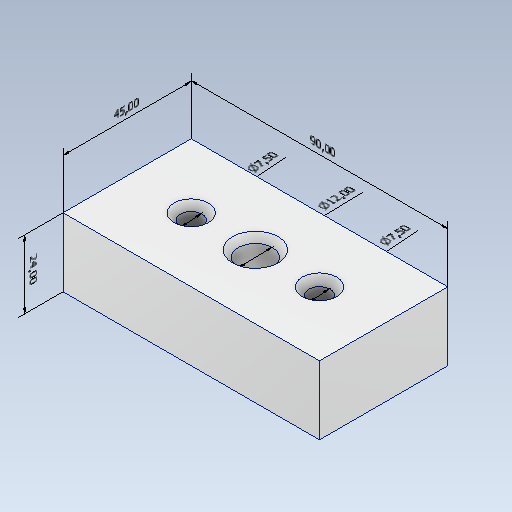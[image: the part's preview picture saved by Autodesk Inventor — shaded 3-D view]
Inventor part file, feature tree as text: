
AUTODESK INVENTOR PART (.ipt)
format: ipt  version: 2021 (Build 250183000, 183)  size: 139,776 bytes
history: native  units: mm
features: other x9, sketch x4, hole x3, extrude x1
ambient origin geometry x8: Origin, YZ Plane, XZ Plane, XY Plane, X Axis, Y Axis, Z Axis, Center Point
bodies: Body1 (feature_tree)
feature tree (17):
  other  "sujecion_castor"
  other  "Sólido1"
  other  "Anotaciones"
  extrude  "Extrusión1"  [1 undecoded]
  hole  "Agujero1"  [1 undecoded]
  hole  "Agujero2"  [1 undecoded]
  hole  "Agujero3"  [1 undecoded]
  sketch  "Boceto1"  dims[d5=24.0mm d6=0.0mm]
  sketch  "Boceto2"  dims[d7=7.5mm d8=6.0mm d9=12.0mm d10=2.0mm d11=90.0deg d12=8.0mm d13=20.594885mm]
  sketch  "Boceto3"  dims[d14=12.0mm d15=5.94614mm d16=16.0mm d17=2.0mm d18=14.3117mm d19=8.0mm d20=20.594885mm]
  sketch  "Boceto4"  dims[d21=7.5mm d22=5.94614mm d23=12.0mm d24=2.0mm d25=14.3117mm d26=8.0mm d27=20.594885mm d28=0.0mm d29=10.0mm d30=24.0mm d31=0.0mm d32=10.0mm d33=45.0mm d34=0.0mm d35=10.0mm d36=90.0mm d43=16.427265mm d44=7.5mm d45=15.948818mm d46=12.0mm d47=16.354086mm d48=7.5mm]
  other  "Cota lineal 1"
  other  "Cota lineal 2"
  other  "Cota lineal 3"
  other  "Cota de diámetro 1"
  other  "Cota de diámetro 2"
  other  "Cota de diámetro 3"
note: 4 required parameter values undecoded (feature->parameter linkage not recoverable at this tier; creation-order binding heuristic only, values carry confidence <= 0.55)
